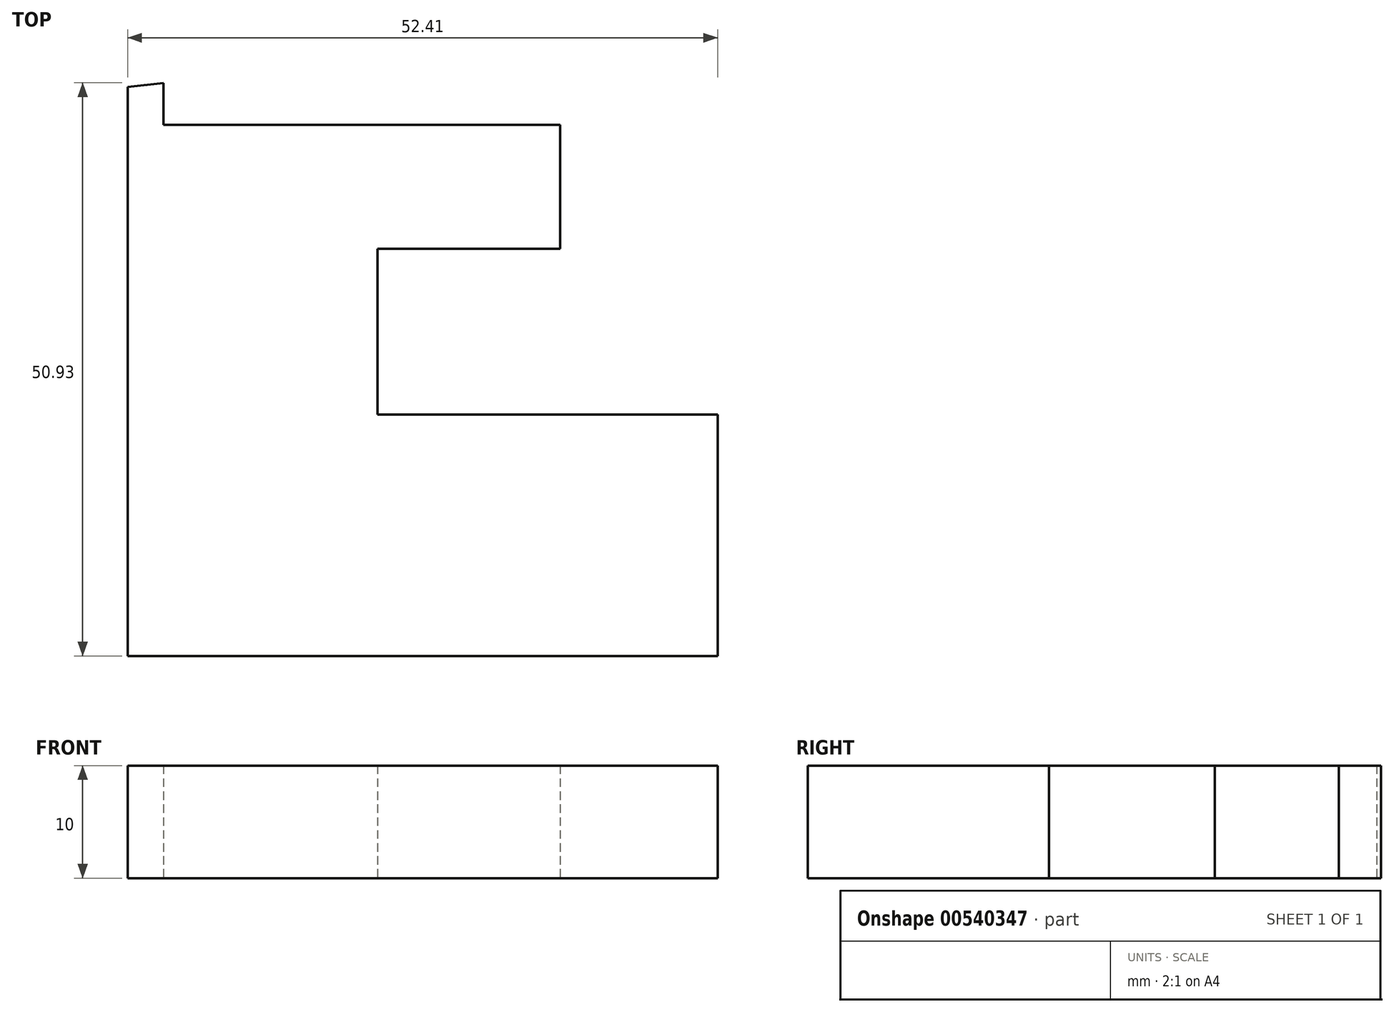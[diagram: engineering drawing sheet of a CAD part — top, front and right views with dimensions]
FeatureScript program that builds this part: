
annotation { "Feature Type Name" : "Feature", "Feature Type Description" : "" }
export const myFeature = defineFeature(function(context is Context, id is Id, definition is map)
    precondition{}
    {
        {
            var Q0;
            Q0=qCreatedBy(makeId("Top.planeOp"),FACE);
            var sketch = newSketch(context, id + "F0", { "sketchPlane" : qUnion([Q0])});
            skLineSegment(sketch, "E0", {"start": v(-24.6, 24.33) * mm, "end": v(-24.6, -26.22) * mm});
            skLineSegment(sketch, "E1", {"start": v(-24.6, -26.22) * mm, "end": v(27.81, -26.22) * mm});
            skLineSegment(sketch, "E2", {"start": v(27.81, -26.22) * mm, "end": v(27.81, -4.77) * mm});
            skLineSegment(sketch, "E3", {"start": v(27.81, -4.77) * mm, "end": v(-2.4, -4.77) * mm});
            skLineSegment(sketch, "E4", {"start": v(-2.4, -4.77) * mm, "end": v(-2.4, 9.97) * mm});
            skLineSegment(sketch, "E5", {"start": v(-2.4, 9.97) * mm, "end": v(13.83, 9.97) * mm});
            skLineSegment(sketch, "E6", {"start": v(13.83, 9.97) * mm, "end": v(13.83, 20.98) * mm});
            skLineSegment(sketch, "E7", {"start": v(13.83, 20.98) * mm, "end": v(-21.43, 20.98) * mm});
            skLineSegment(sketch, "E8", {"start": v(-21.43, 20.98) * mm, "end": v(-21.43, 24.7) * mm});
            skLineSegment(sketch, "E9", {"start": v(-21.43, 24.7) * mm, "end": v(-24.6, 24.33) * mm});
            skSolve(sketch);
        }
        {
            var Q0;
            Q0=makeQuery(id+"F0.imprint","IMPRINT",FACE,{"disambiguationData":[TD([[makeQuery(id+"F0.imprint","IMPRINT",EDGE,{"derivedFrom":sQuery(id+"F0.wireOp",EDGE,"E0")}),1.0]])]});
            extrude(context, id + "F1", {"entities" : qUnion([Q0]), "depth" : 10 * mm, "offsetDistance" : 25 * mm});
        }
    });
